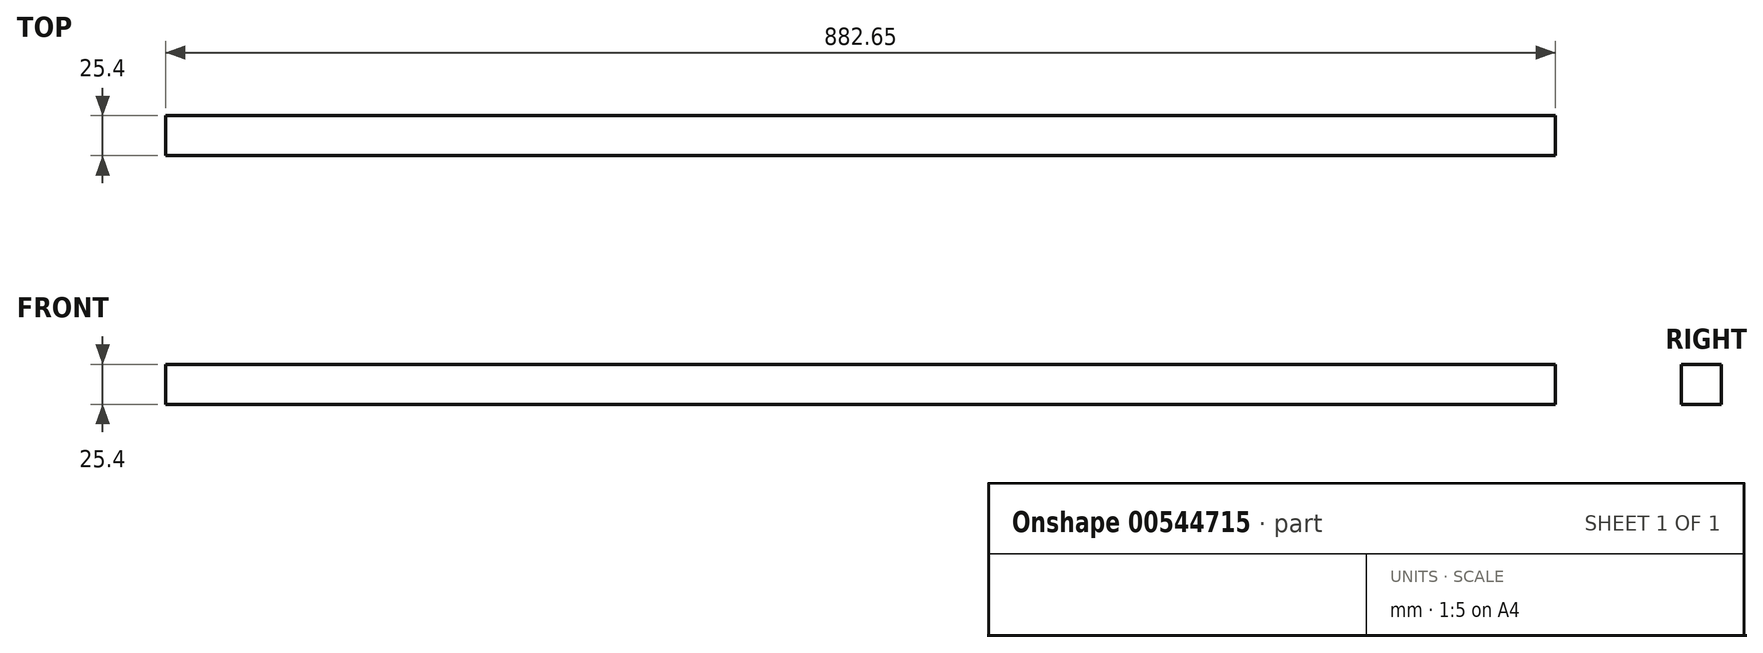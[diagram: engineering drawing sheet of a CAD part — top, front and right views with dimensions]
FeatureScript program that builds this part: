
annotation { "Feature Type Name" : "Feature", "Feature Type Description" : "" }
export const myFeature = defineFeature(function(context is Context, id is Id, definition is map)
    precondition{}
    {
        {
            var Q0;
            Q0=qCreatedBy(makeId("Top.planeOp"),FACE);
            var sketch = newSketch(context, id + "F0", { "sketchPlane" : qUnion([Q0])});
            skLineSegment(sketch, "E0.bottom", {"start": v(0, 0) * mm, "end": v(882.65, 0) * mm});
            skLineSegment(sketch, "E0.top", {"start": v(0, 25.4) * mm, "end": v(882.65, 25.4) * mm});
            skLineSegment(sketch, "E0.left", {"start": v(0, 0) * mm, "end": v(0, 25.4) * mm});
            skLineSegment(sketch, "E0.right", {"start": v(882.65, 0) * mm, "end": v(882.65, 25.4) * mm});
            skSolve(sketch);
        }
        {
            var Q0;
            Q0=makeQuery(id+"F0.imprint","IMPRINT",FACE,{"disambiguationData":[TD([[makeQuery(id+"F0.imprint","IMPRINT",EDGE,{"derivedFrom":sQuery(id+"F0.wireOp",EDGE,"E0.bottom")}),1.0]])]});
            extrude(context, id + "F1", {"entities" : qUnion([Q0]), "depth" : 25.4 * mm, "offsetDistance" : 25.4 * mm});
        }
    });
